# Revit family: floodlight_fl_11_maxi_remote___pl64_5xa779514e01ba_6d82
name_source: partatom
category: Lighting Fixtures
units: mm (PartAtom-declared; Revit-internal decimal feet)

## family parameters
Cut with Voids When Loaded = No
Host = Face
Light Source = No
Part Type = Normal
Room Calculation Point = No
Round Connector Dimension = Use Diameter
Shared = No

## types (1)
- --- (1 x LED, 74800 lm, 707.9 W, 5700K)
    Apparent Load = 708 VA
    CIE Flux Codes = 28 80 98 100 100
    Color Rendering = 90
    Color Temperature = 5700K
    Default Elevation = 1800 mm
    Description = Floodlight FL 11  maxi  Remote floodlight; light control with lens of PMMA; cover panel of toughened safety glass, transparent; light distribution: PL64, asymmetric direct distribution, LEDcolour temperature: 5700K, rated luminous flux: 74.800lm, colour rendering: CRI > 90, light colour: 957; luminous efficacy: 106lm/W; brightness control: DMX+RDM; with terminal, 8-pole, max. 2.5mm², mains connection: 220..240V/380..400V AC, 50/60Hz, surge voltage resistance: line to ground: 10kV, ECG replaceable separately, LED unit replaceable without ESD environment, dustproof LED module, dimming range 10..100%; 708W floodlight with 2x LED unit of diecast aluminium, coated grey; length: 713mm / width: 651mm / height: 338mm; mounting bracket, of diecast aluminium, uncoated, natural, equipment: Longlife, protection rating (complete): IP66; insulation class (complete): insulation class I (protective earthing); certification: CE, ENEC, VDE; ball protection: ball impact resistance with accessories, impact resistance: IK07; only for outdoor installations, rated ambient temperature 10°C, permissible operating ambient temperature: -40..+40°C, permissible storage temperature: -40..+85°C; packaging unit: 1 piece

Light Distribution: PL64
    Height = 320 mm
    Lamp = 1 x LED
    Lamp Light Flux = 74800 lm
    Lamp Power = 707.9 W
    Lamp count = 1
    Length = 712 mm
    Luminous efficacy = 106 lm/W
    Manufacturer = Siteco
    ModVariant = No
    Model = 5XA779514E01BA
    Mounting Place = Ceiling
    Mounting Type = Surface mounted
    Number of Poles = 1
    OnlyDefault = Yes
    Power Factor = 1
    Product Name = Floodlight FL 11 maxi Remote | PL64
    Product group = floodlight | ceiling mounted
    ProductGroupID = 302
    Protection Class = Protection class I
    Protection Degree = IP 66
    RLX_Detail_Level = 1
    RLX_Emergency_Light_Flux = 0 lm
    RLX_Emergency_Type = 0
    RLX_Emergency_Type_DB = No
    RlxData = <blob elided: 46561 chars, md5=1c5b5ca8>
    Socket = socket
    Standby Power = 0 W
    System Light Flux = 74800 lm
    System Power = 708 W
    Type Comments = factory setting: luminous flux: 100 % | dim-lin: 254 | 740 mA
    Type Image = l_1006788.jpg
    URL = http://relux.com
    VarID = @adj_152685
    Voltage = 0 V
    Weight = 0.00 kg
    Width = 655 mm

## geometry (parser evidence)
native form markers: Sweep x15
no freeform markers — native parametric forms only
